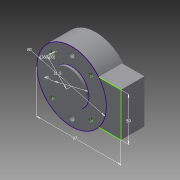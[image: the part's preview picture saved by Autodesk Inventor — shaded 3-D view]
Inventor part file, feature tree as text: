
AUTODESK INVENTOR PART (.ipt)
format: ipt  version: 2013 (Build 170138000, 138)  size: 115,712 bytes
history: native  units: mm
features: extrude x4, sketch x2, hole x2
ambient origin geometry x8: Origin, YZ Plane, XZ Plane, XY Plane, X Axis, Y Axis, Z Axis, Center Point
bodies: Solid1 (feature_tree)
feature tree (8):
  sketch  "Sketch1"  dims[d0=80.0mm d2=40.0mm]
  extrude  "Extrusion1"  Depth=40.0mm
  extrude  "Extrusion2"  Depth=50.0mm
  extrude  "Extrusion3"  Depth=31.5mm
  extrude  "Extrusion4"  Depth=40.0mm TaperAngle=360.0deg
  hole  "Hole1"  [1 undecoded]
  hole  "Hole2"  [1 undecoded]
  sketch  "Sketch2"  dims[d5=97.0mm d6=50.0mm d7=31.5mm d8=40.0mm d10=360.0deg d12=28.0mm d13=0.0mm d14=28.0mm d15=0.0mm d16=3.0mm d17=0.0mm d18=27.0mm d19=0.0mm d20=5.459mm d21=6.0mm d22=14.55mm d23=4.38mm d24=90.0deg d25=8.0mm d26=20.594885mm d27=31.5mm d28=20.0mm d30=360.0deg d32=6.6mm d33=6.0mm d34=14.55mm d35=4.38mm d36=90.0deg d37=8.0mm d38=20.594885mm]
note: 2 required parameter values undecoded (feature->parameter linkage not recoverable at this tier; creation-order binding heuristic only, values carry confidence <= 0.55)
